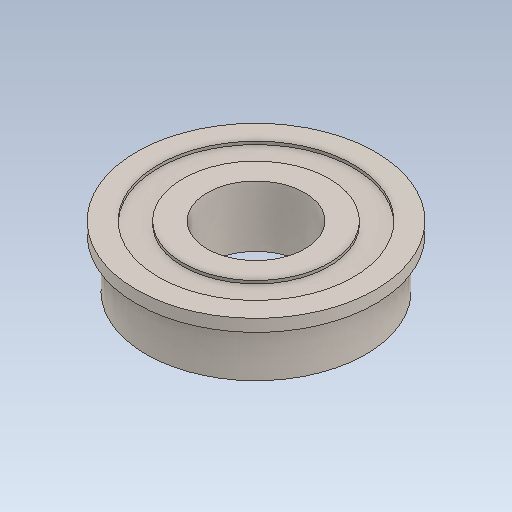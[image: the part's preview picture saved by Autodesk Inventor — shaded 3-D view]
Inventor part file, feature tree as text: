
AUTODESK INVENTOR PART (.ipt)
format: ipt  version: 2020 (Build 240168000, 168)  size: 125,952 bytes
history: native  units: in
note: dims shown in document units (in); Inventor stores cm internally (conversion verified against a paired STEP export)
features: revolve x1
ambient origin geometry x8: Origin, YZ Plane, XZ Plane, XY Plane, X Axis, Y Axis, Z Axis, Center Point
bodies: Solid1 (feature_tree)
feature tree (1):
  revolve  "Revolve1"  [1 undecoded]
note: 1 required parameter value undecoded (feature->parameter linkage not recoverable at this tier; creation-order binding heuristic only, values carry confidence <= 0.55)
